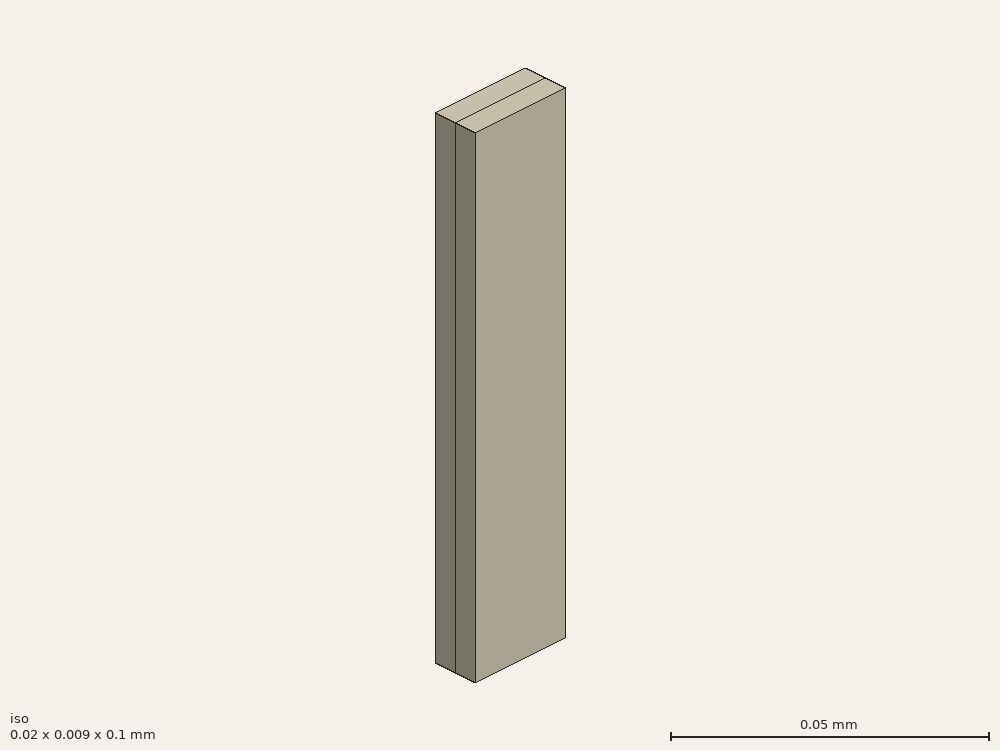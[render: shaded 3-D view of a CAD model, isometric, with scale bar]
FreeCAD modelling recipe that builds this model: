
FCSTD DOCUMENT  (FreeCAD 0.21R33694 (Git))
Label: partially_filled_waveguide
License: All rights reserved
LicenseURL: http://en.wikipedia.org/wiki/All_rights_reserved
objects: Part::Part2DObjectPython×10, App::FeaturePython×8, Part::Extrusion×2, Part::FeaturePython×1
note: 13 computed .brp shape members not serialized (recipe doc carries the construction recipe); baked Part::Feature solids carry a one-line shape summary decoded from their .brp

FEATURE [Part::Part2DObjectPython] Rectangle  label="air"  # Draft 2D object (typed FeaturePython)
  Area = 9e-05
  ChamferSize = 0
  Columns = 1
  FilletRadius = 0
  Height = 0.0045
  Length = 0.02
  MakeFace = true
  Placement = pos=(0,0.0045,0) rot=(0,0,1;0rad)
  Rows = 1
FEATURE [Part::Part2DObjectPython] Rectangle001  label="teflon"  # Draft 2D object (typed FeaturePython)
  Area = 9e-05
  ChamferSize = 0
  Columns = 1
  FilletRadius = 0
  Height = 0.0045
  Length = 0.02
  MakeFace = true
  Rows = 1
FEATURE [Part::Extrusion] Extrude
  Base = -> Rectangle
  Dir = (0,0,1)
  DirMode = 2
  FaceMakerClass = Part::FaceMakerBullseye
  LengthFwd = 0.1
  LengthRev = 0
  Solid = false
  Symmetric = false
FEATURE [Part::Extrusion] Extrude001
  Base = -> Rectangle001
  Dir = (0,0,1)
  DirMode = 2
  FaceMakerClass = Part::FaceMakerBullseye
  LengthFwd = 0.1
  LengthRev = 0
  Solid = false
  Symmetric = false
FEATURE [Part::FeaturePython] BooleanFragments  # WARN: FeaturePython — macro-defined, semantics opaque (R4)
  Mode = 0
  Objects = -> [Extrude001,Extrude]
  Tolerance = 0
FEATURE [Part::Part2DObjectPython] Rectangle003  label="_P2"  # Draft 2D object (typed FeaturePython)
  Area = 0.00018
  ChamferSize = 0
  Columns = 1
  FilletRadius = 0
  Height = 0.009
  Length = 0.02
  MakeFace = true
  Placement = pos=(0,0,0.1) rot=(0,0,1;0rad)
  Rows = 1
FEATURE [Part::Part2DObjectPython] Line001  label="_Pv2"  # Draft 2D object (typed FeaturePython)
  Area = 0
  ChamferSize = 0
  Closed = false
  End = (0.01,0.009,0.1)
  FilletRadius = 0
  Length = 0.009
  MakeFace = true
  Placement = pos=(0.01,0,0.1) rot=(0,0,1;0rad)
  Points = (2) [(0,0,0),(0,0.009,0)]
  Start = (0.01,0,0.1)
  Subdivisions = 0
FEATURE [App::FeaturePython] Text  label="_S1(PV){1}"  # WARN: FeaturePython — macro-defined, semantics opaque (R4)
  Placement = pos=(0.0691109,-0.0323124,0) rot=(0,0,1;0rad)
  Text = .
FEATURE [App::FeaturePython] Text001  label="_S2(PV){2}"  # WARN: FeaturePython — macro-defined, semantics opaque (R4)
  Placement = pos=(0.0691109,-0.0323124,0) rot=(0,0,1;0rad)
  Text = .
FEATURE [App::FeaturePython] Text002  label="_L1(1,voltage){v1}"  # WARN: FeaturePython — macro-defined, semantics opaque (R4)
  Placement = pos=(0.0691109,-0.0323124,0) rot=(0,0,1;0rad)
  Text = .
FEATURE [App::FeaturePython] Text003  label="_L2(2,voltage){v2}"  # WARN: FeaturePython — macro-defined, semantics opaque (R4)
  Placement = pos=(0.0691109,-0.0323124,0) rot=(0,0,1;0rad)
  Text = .
FEATURE [Part::Part2DObjectPython] Rectangle004  label="_P1"  # Draft 2D object (typed FeaturePython)
  Area = 0.00018
  ChamferSize = 0
  Columns = 1
  FilletRadius = 0
  Height = 0.009
  Length = 0.02
  MakeFace = true
  Rows = 1
FEATURE [Part::Part2DObjectPython] Line  label="_Pv1"  # Draft 2D object (typed FeaturePython)
  Area = 0
  ChamferSize = 0
  Closed = false
  End = (0.01,0.009,0)
  FilletRadius = 0
  Length = 0.009
  MakeFace = true
  Placement = pos=(0.01,0,0) rot=(0,0,1;0rad)
  Points = (2) [(0,0,0),(0,0.009,0)]
  Start = (0.01,0,0)
  Subdivisions = 0
FEATURE [Part::Part2DObjectPython] Rectangle005  label="_Pb"  # Draft 2D object (typed FeaturePython)
  Area = 0.002
  ChamferSize = 0
  Columns = 1
  FilletRadius = 0
  Height = 0.1
  Length = 0.02
  MakeFace = true
  Placement = pos=(0,0,0) rot=(1,0,0;1.5708rad)
  Rows = 1
FEATURE [Part::Part2DObjectPython] Rectangle006  label="_Pt"  # Draft 2D object (typed FeaturePython)
  Area = 0.002
  ChamferSize = 0
  Columns = 1
  FilletRadius = 0
  Height = 0.1
  Length = 0.02
  MakeFace = true
  Placement = pos=(0,0.009,0) rot=(1,0,0;1.5708rad)
  Rows = 1
FEATURE [Part::Part2DObjectPython] Rectangle007  label="_Pr"  # Draft 2D object (typed FeaturePython)
  Area = 0.0009
  ChamferSize = 0
  Columns = 1
  FilletRadius = 0
  Height = 0.1
  Length = 0.009
  MakeFace = true
  Placement = pos=(0.02,0,0) rot=(0.57735,0.57735,0.57735;2.0944rad)
  Rows = 1
FEATURE [Part::Part2DObjectPython] Rectangle008  label="_Pl"  # Draft 2D object (typed FeaturePython)
  Area = 0.0009
  ChamferSize = 0
  Columns = 1
  FilletRadius = 0
  Height = 0.1
  Length = 0.009
  MakeFace = true
  Placement = pos=(0,0,0) rot=(0.57735,0.57735,0.57735;2.0944rad)
  Rows = 1
FEATURE [App::FeaturePython] Text004  label="_Bt(SI,copper){t}"  # WARN: FeaturePython — macro-defined, semantics opaque (R4)
  Placement = pos=(0.0691109,-0.0323124,0) rot=(0,0,1;0rad)
  Text = .
FEATURE [App::FeaturePython] Text005  label="_Bb(SI,copper){b}"  # WARN: FeaturePython — macro-defined, semantics opaque (R4)
  Placement = pos=(0.0691109,-0.0323124,0) rot=(0,0,1;0rad)
  Text = .
FEATURE [App::FeaturePython] Text006  label="_Br(SI,copper){r}"  # WARN: FeaturePython — macro-defined, semantics opaque (R4)
  Placement = pos=(0.0691109,-0.0323124,0) rot=(0,0,1;0rad)
  Text = .
FEATURE [App::FeaturePython] Text007  label="_Bl(SI,copper){l}"  # WARN: FeaturePython — macro-defined, semantics opaque (R4)
  Placement = pos=(0.0691109,-0.0323124,0) rot=(0,0,1;0rad)
  Text = .
